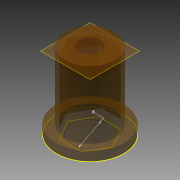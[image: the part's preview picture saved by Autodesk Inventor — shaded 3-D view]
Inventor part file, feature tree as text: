
AUTODESK INVENTOR PART (.ipt)
format: ipt  version: 2014 (Build 180170000, 170)  size: 143,872 bytes
history: native  units: mm
features: sketch x6, extrude x3, hole x1, plane x1, revolve x1, chamfer x1, projected_geometry x1
ambient origin geometry x8: Origin, YZ Plane, XZ Plane, XY Plane, X Axis, Y Axis, Z Axis, Center Point
bodies: Solid1 (feature_tree)
feature tree (14):
  extrude  "Extrusion1"  Depth=2.0mm TaperAngle=0.0deg
  extrude  "Extrusion2"  Depth=15.0mm TaperAngle=0.0deg
  hole  "Hole1"  [1 undecoded]
  plane  "Work Plane1"
  extrude  "Extrusion3"  Depth=10.0mm TaperAngle=0.0deg
  sketch  "Sketch6"  dims[d17=8.0mm d18=45.0deg]
  revolve  "Revolution1"  Angle=45.0deg
  chamfer  "Chamfer1"  Distance=2.0mm Angle=45.0deg
  sketch  "Sketch2"  dims[d0=15.0mm d1=2.0mm d2=0.0mm]
  sketch  "Sketch3"  dims[d3=11.0mm d4=15.0mm d5=0.0mm]
  sketch  "Sketch4"  dims[d6=4.7mm d7=6.0mm d8=7.087mm d9=4.775mm d10=14.3117mm d11=8.0mm d12=20.594885mm d13=-1.0mm]
  sketch  "Sketch5"  dims[d14=8.6375mm d15=10.0mm d16=0.0mm]
  sketch  "Sketch7"  dims[d19=90.0deg d20=2.0mm d21=2.0mm d22=45.0deg]
  projected_geometry  "Project Cut Edges1"
note: 1 required parameter value undecoded (feature->parameter linkage not recoverable at this tier; creation-order binding heuristic only, values carry confidence <= 0.55)
